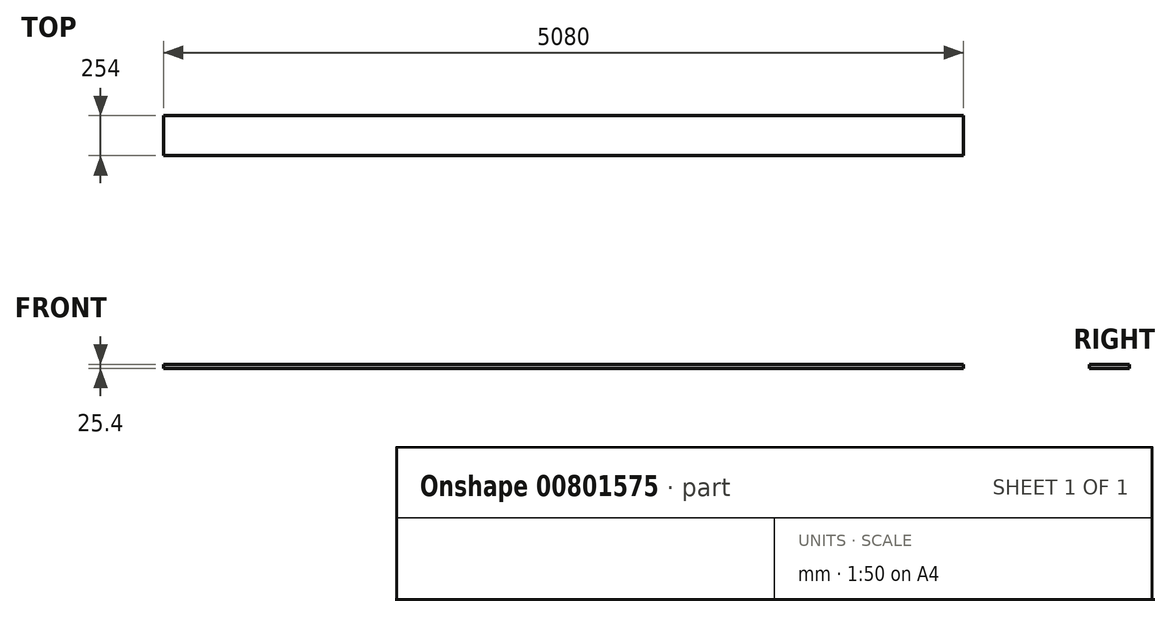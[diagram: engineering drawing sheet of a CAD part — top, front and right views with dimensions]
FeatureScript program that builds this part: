
annotation { "Feature Type Name" : "Feature", "Feature Type Description" : "" }
export const myFeature = defineFeature(function(context is Context, id is Id, definition is map)
    precondition{}
    {
        {
            var Q0;
            Q0=qCreatedBy(makeId("Top.planeOp"),FACE);
            var sketch = newSketch(context, id + "F0", { "sketchPlane" : qUnion([Q0])});
            skLineSegment(sketch, "E0.bottom", {"start": v(-39.4, 231.35) * mm, "end": v(5040.6, 231.35) * mm});
            skLineSegment(sketch, "E0.top", {"start": v(-39.4, -22.65) * mm, "end": v(5040.6, -22.65) * mm});
            skLineSegment(sketch, "E0.left", {"start": v(-39.4, 231.35) * mm, "end": v(-39.4, -22.65) * mm});
            skLineSegment(sketch, "E0.right", {"start": v(5040.6, 231.35) * mm, "end": v(5040.6, -22.65) * mm});
            skSolve(sketch);
        }
        {
            var Q0;
            Q0 = qSketchRegion(id + "F0", true);
            extrude(context, id + "F1", {"entities" : qUnion([Q0]), "depth" : 25.4 * mm, "offsetDistance" : 25.4 * mm});
        }
    });
